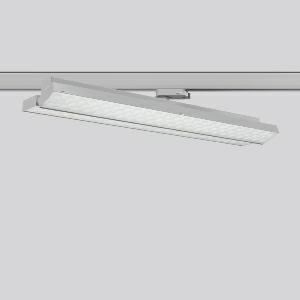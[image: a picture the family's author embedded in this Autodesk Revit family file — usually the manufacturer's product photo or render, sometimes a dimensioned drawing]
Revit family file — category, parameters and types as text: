
# Revit family: tx-move_742161_004_3_76_4e08
name_source: partatom
category: Lighting Fixtures
units: mm (PartAtom-declared; Revit-internal decimal feet)

## family parameters
Cut with Voids When Loaded = No
Host = Face
Light Source = No
Part Type = Normal
Room Calculation Point = No
Round Connector Dimension = Use Diameter
Shared = No

## types (1)
- MultiLumen 1 (1 x LED Modul 835, 3025 lm, 3500)
    Apparent Load = 41 VA
    CIE Flux Codes = 88 96 99 100 100
    Color Rendering = 80
    Color Temperature = 3500
    Default Elevation = 1800 mm
    Description = Series: TX-MOVE
Multifunctional surface-mounted spotlight for area lighting. Very flat design. Housing: sheet steel, powder-coated. Rotation range: 356°. Swivel range: 90°. Consistent alignment possible with visible tilt scale. High-efficiency LED units with optimum light control thanks to clear plastic (PC) lens optics. Spezielle Mikrostrukturen reduzieren Gelbsaum. Symmetrical light distribution. With adapter for RZB 3-circuit DALI tracks. Suitable for Track on ceiling. MultiLumen: Luminous flux adjustable in 3 steps. Factory setting is the highest luminous flux. Environmentally friendly and resource-saving due to replaceable and recyclable components. 
Colour: silver, matt (approx. RAL 9006)
Length: 570 mm
Width: 119 mm
Height: 88 mm
Lamp: LED
Socket: without socket
Colour temperature: 3500K
Colour rendering index (CRI): 80
System power: 41 W
Rated luminous flux: 6050 lm
Luminous efficiency: 148 lm/W
System power 2: 57 W
Rated luminous flux 2: 8200 lm
Luminous efficiency 2: 144 lm/W
System power 3: 73 W
Rated luminous flux 3: 10000 lm
Luminous efficiency 3: 137 lm/W
Control gear: Dimmable EVG, DALI
Protection class: I
Type of protection: IP 20
    Height = 75 mm
    Lamp = 1 x LED Modul 835
    Lamp Light Flux = 3025 lm
    Lamp count = 1
    Length = 569 mm
    Lifetime = 50000 h
    Luminous efficacy = 148 lm/W
    Manufacturer = RZB
    ModVariant = No
    Model = 742161.004.3.76
    Mounting Place = Ceiling
    Mounting Type = Rail mounted
    Number of Poles = 1
    OnlyDefault = Yes
    Power Factor = 1
    Product Name = TX-MOVE
    Product group = Track mounted projectors
    ProductGroupID = 301
    Protection Class = Protection class I
    Protection Degree = IP 20
    RLX_Detail_Level = 1
    RLX_Emergency_Light_Flux = 0 lm
    RLX_Emergency_Type = 0
    RLX_Emergency_Type_DB = No
    RlxData = <blob elided: 33337 chars, md5=508153bc>
    Socket = socket
    Standby Power = 0 W
    System Light Flux = 6050 lm
    System Power = 41 W
    Type Comments = MultiLumen 1
    Type Image = 742162.004.jpg
    URL = http://relux.com
    VarID = multilumen_1
    Voltage = 230 V
    Voltage Range = 220-240 V
    Weight = 0.00 kg
    Width = 119 mm

## geometry (parser evidence)
native form markers: Blend x4, Sweep x15
no freeform markers — native parametric forms only
